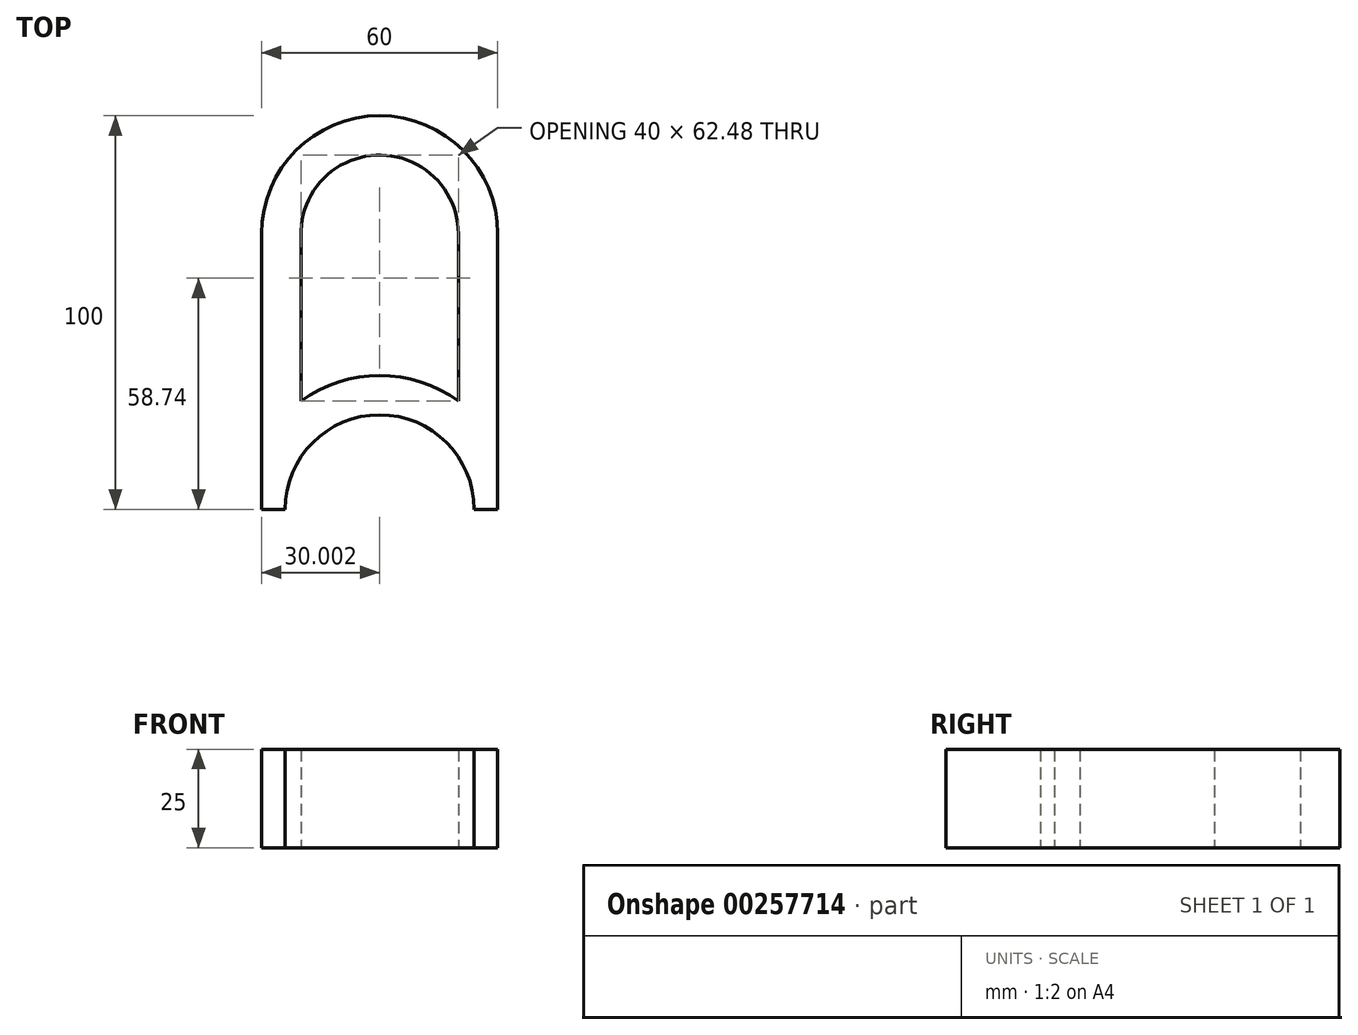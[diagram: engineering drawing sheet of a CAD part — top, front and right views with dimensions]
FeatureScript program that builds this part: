
annotation { "Feature Type Name" : "Feature", "Feature Type Description" : "" }
export const myFeature = defineFeature(function(context is Context, id is Id, definition is map)
    precondition{}
    {
        {
            var Q0;
            Q0=qCreatedBy(makeId("Top.planeOp"),FACE);
            var sketch = newSketch(context, id + "F0", { "sketchPlane" : qUnion([Q0])});
            skLineSegment(sketch, "E0", {"start": v(66.96, -19.64) * mm, "end": v(66.96, 50.36) * mm});
            skLineSegment(sketch, "E1", {"start": v(36.96, 80.36) * mm, "end": v(36.96, 80.36) * mm});
            skLineSegment(sketch, "E2", {"start": v(6.96, 50.36) * mm, "end": v(6.96, -19.64) * mm});
            skLineSegment(sketch, "E3", {"start": v(6.96, -19.64) * mm, "end": v(12.96, -19.64) * mm});
            skLineSegment(sketch, "E4", {"start": v(66.96, -19.64) * mm, "end": v(60.96, -19.64) * mm});
            skPoint(sketch, "E5.visualSharp", {"position": v(6.96, 80.36) * mm});
            skArc(sketch, "E5.filletArc", {"start": v(36.96, 80.36) * mm, "mid": v(15.75, 71.58) * mm, "end": v(6.96, 50.36) * mm});
            skPoint(sketch, "E6.visualSharp", {"position": v(66.96, 80.36) * mm});
            skArc(sketch, "E6.filletArc", {"start": v(66.96, 50.36) * mm, "mid": v(58.18, 71.58) * mm, "end": v(36.96, 80.36) * mm});
            skArc(sketch, "E7", {"start": v(60.96, -19.64) * mm, "mid": v(36.96, 4.36) * mm, "end": v(12.96, -19.64) * mm});
            skArc(sketch, "E8", {"start": v(56.96, 7.86) * mm, "mid": v(36.96, 14.36) * mm, "end": v(16.96, 7.86) * mm});
            skLineSegment(sketch, "E9", {"start": v(16.96, 10.36) * mm, "end": v(16.96, 7.86) * mm});
            skLineSegment(sketch, "E10", {"start": v(56.96, 18.06) * mm, "end": v(56.96, 7.86) * mm});
            skArc(sketch, "E11", {"start": v(56.96, 50.36) * mm, "mid": v(36.03, 70.34) * mm, "end": v(17.05, 48.5) * mm});
            skLineSegment(sketch, "E12", {"start": v(16.96, 10.36) * mm, "end": v(17.05, 48.5) * mm});
            skLineSegment(sketch, "E13", {"start": v(56.96, 18.06) * mm, "end": v(56.96, 50.36) * mm});
            skSolve(sketch);
        }
        {
            var Q0;
            Q0 = qSketchRegion(id + "F0", true);
            extrude(context, id + "F1", {"entities" : qUnion([Q0]), "depth" : 25 * mm});
        }
    });
